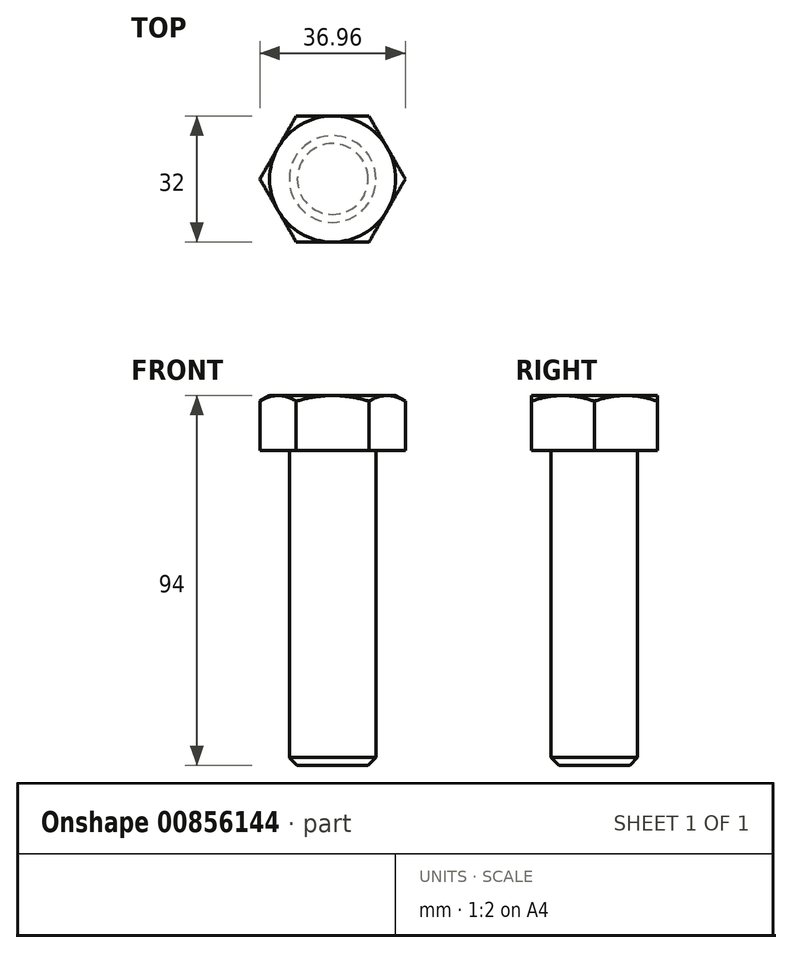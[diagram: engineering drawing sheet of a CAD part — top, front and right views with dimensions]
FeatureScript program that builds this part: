
annotation { "Feature Type Name" : "Feature", "Feature Type Description" : "" }
export const myFeature = defineFeature(function(context is Context, id is Id, definition is map)
    precondition{}
    {
        {
            var Q0;
            Q0=qCreatedBy(makeId("Top.planeOp"),FACE);
            var sketch = newSketch(context, id + "F0", { "sketchPlane" : qUnion([Q0])});
            skCircle(sketch, "E0.cCircle", {"center": v(0, 0) * mm, "radius": 16 * mm, "construction": true});
            skLineSegment(sketch, "E0.0", {"start": v(9.24, 16) * mm, "end": v(18.48, 0) * mm});
            skLineSegment(sketch, "E0.1", {"start": v(18.48, 0) * mm, "end": v(9.24, -16) * mm});
            skLineSegment(sketch, "E0.2", {"start": v(9.24, -16) * mm, "end": v(-9.24, -16) * mm});
            skLineSegment(sketch, "E0.3", {"start": v(-9.24, -16) * mm, "end": v(-18.48, 0) * mm});
            skLineSegment(sketch, "E0.4", {"start": v(-18.48, 0) * mm, "end": v(-9.24, 16) * mm});
            skLineSegment(sketch, "E0.5", {"start": v(-9.24, 16) * mm, "end": v(9.24, 16) * mm});
            skPoint(sketch, "E0.0.midPoint", {"position": v(13.86, 8) * mm});
            skSolve(sketch);
        }
        {
            var Q0;
            Q0=makeQuery(id+"F0.imprint","IMPRINT",FACE,{"disambiguationData":[TD([[makeQuery(id+"F0.imprint","IMPRINT",EDGE,{"derivedFrom":sQuery(id+"F0.wireOp",EDGE,"E0.0")}),-1.0]])]});
            extrude(context, id + "F1", {"entities" : qUnion([Q0]), "depth" : 14 * mm, "offsetDistance" : 25 * mm});
        }
        {
            var Q0;
            Q0=qCreatedBy(makeId("Right.planeOp"),FACE);
            var sketch = newSketch(context, id + "F2", { "sketchPlane" : qUnion([Q0])});
            skLineSegment(sketch, "E1", {"start": v(-16, 14) * mm, "end": v(-29.05, 14) * mm});
            skLineSegment(sketch, "E2", {"start": v(-29.05, 14) * mm, "end": v(-29.05, 6.47) * mm});
            skLineSegment(sketch, "E3", {"start": v(-29.05, 6.47) * mm, "end": v(-16, 14) * mm});
            skLineSegment(sketch, "E4", {"start": v(0, 0) * mm, "end": v(0, 20.15) * mm, "construction": true});
            skSolve(sketch);
        }
        {
            var Q0;
            Q0=makeQuery(id+"F2.imprint","IMPRINT",FACE,{"disambiguationData":[TD([[makeQuery(id+"F2.imprint","IMPRINT",EDGE,{"derivedFrom":sQuery(id+"F2.wireOp",EDGE,"E1")}),1.0]])]});
            var Q1;
            Q1=sQuery(id+"F2.wireOp",EDGE,"E4");
            revolve(context, id + "F3", {"operationType" : NewBodyOperationType.REMOVE, "surfaceOperationType" : NewSurfaceOperationType.NEW, "entities" : qUnion([Q0]), "axis" : qUnion([Q1]), "revolveType" : RevolveType.FULL, "oppositeDirection" : true});
        }
        {
            var Q0;
            Q0=makeQuery(id+"F1.opExtrude","CAP_FACE",FACE,{"disambiguationData":[OSD([sQuery(id+"F0.wireOp",EDGE,"E0.0"),sQuery(id+"F0.wireOp",EDGE,"E0.1"),sQuery(id+"F0.wireOp",EDGE,"E0.2"),sQuery(id+"F0.wireOp",EDGE,"E0.3"),sQuery(id+"F0.wireOp",EDGE,"E0.4"),sQuery(id+"F0.wireOp",EDGE,"E0.5")])],"isStart":true});
            var sketch = newSketch(context, id + "F4", { "sketchPlane" : qUnion([Q0])});
            skCircle(sketch, "E5", {"center": v(0, 0) * mm, "radius": 11 * mm});
            skSolve(sketch);
        }
        {
            var Q0;
            Q0=makeQuery(id+"F4.imprint","IMPRINT",FACE,{"disambiguationData":[TD([[makeQuery(id+"F4.imprint","IMPRINT",EDGE,{"derivedFrom":sQuery(id+"F4.wireOp",EDGE,"E5")}),1.0]])]});
            extrude(context, id + "F5", {"entities" : qUnion([Q0]), "operationType" : NewBodyOperationType.ADD, "depth" : 80 * mm, "offsetDistance" : 25 * mm});
        }
        {
            var Q0;
            Q0=makeQuery(id+"F5.opExtrude","CAP_EDGE",EDGE,{"disambiguationData":[OSD([sQuery(id+"F4.wireOp",EDGE,"E5")])],"isStart":false});
            chamfer(context, id + "F6", {"entities" : qUnion([Q0]), "width" : 2 * mm, "tangentPropagation" : true});
        }
    });
